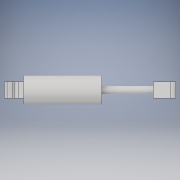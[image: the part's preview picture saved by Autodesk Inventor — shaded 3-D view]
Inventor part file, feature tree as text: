
AUTODESK INVENTOR PART (.ipt)
format: ipt  version: 2018 (Build 220112000, 112)  size: 174,080 bytes
history: native  units: mm
features: sketch x6, extrude x6, other x2
ambient origin geometry x8: Origin, YZ Plane, XZ Plane, XY Plane, X Axis, Y Axis, Z Axis, Center Point
bodies: Body1 (feature_tree), Body2 (feature_tree)
feature tree (14):
  other  "ShockBottle"
  sketch  "Sketch12"  dims[d44=8.0mm d45=8.0mm d46=240.0mm d47=6.0mm d48=6.0mm d49=16.0mm d50=4.0mm d51=8.0mm d52=6.0mm d53=24.0mm d54=0.0mm d58=38.0mm]
  extrude  "Extrusion14"  Depth=24.0mm
  extrude  "Extrusion16"  Depth=115.0mm TaperAngle=0.0deg
  extrude  "Extrusion17"  Depth=4.0mm TaperAngle=0.0deg
  extrude  "Extrusion18"  Depth=76.0mm
  extrude  "Extrusion20"  Depth=24.0mm
  extrude  "Extrusion21"  [1 undecoded]
  sketch  "Sketch14"  dims[d59=2.0mm d60=115.0mm d61=0.0mm]
  sketch  "Sketch15"  dims[d62=4.0mm d63=0.0mm d64=4.0mm d65=0.0mm]
  sketch  "Sketch16"  dims[d68=8.0mm d69=8.0mm d71=6.0mm d77=76.0mm]
  sketch  "Sketch17"  dims[d78=24.0mm d79=0.0mm d80=12.0mm]
  sketch  "Sketch18"  dims[d81=24.0mm d82=0.0mm]
  other  "ShockShaft"
note: 1 required parameter value undecoded (feature->parameter linkage not recoverable at this tier; creation-order binding heuristic only, values carry confidence <= 0.55)
